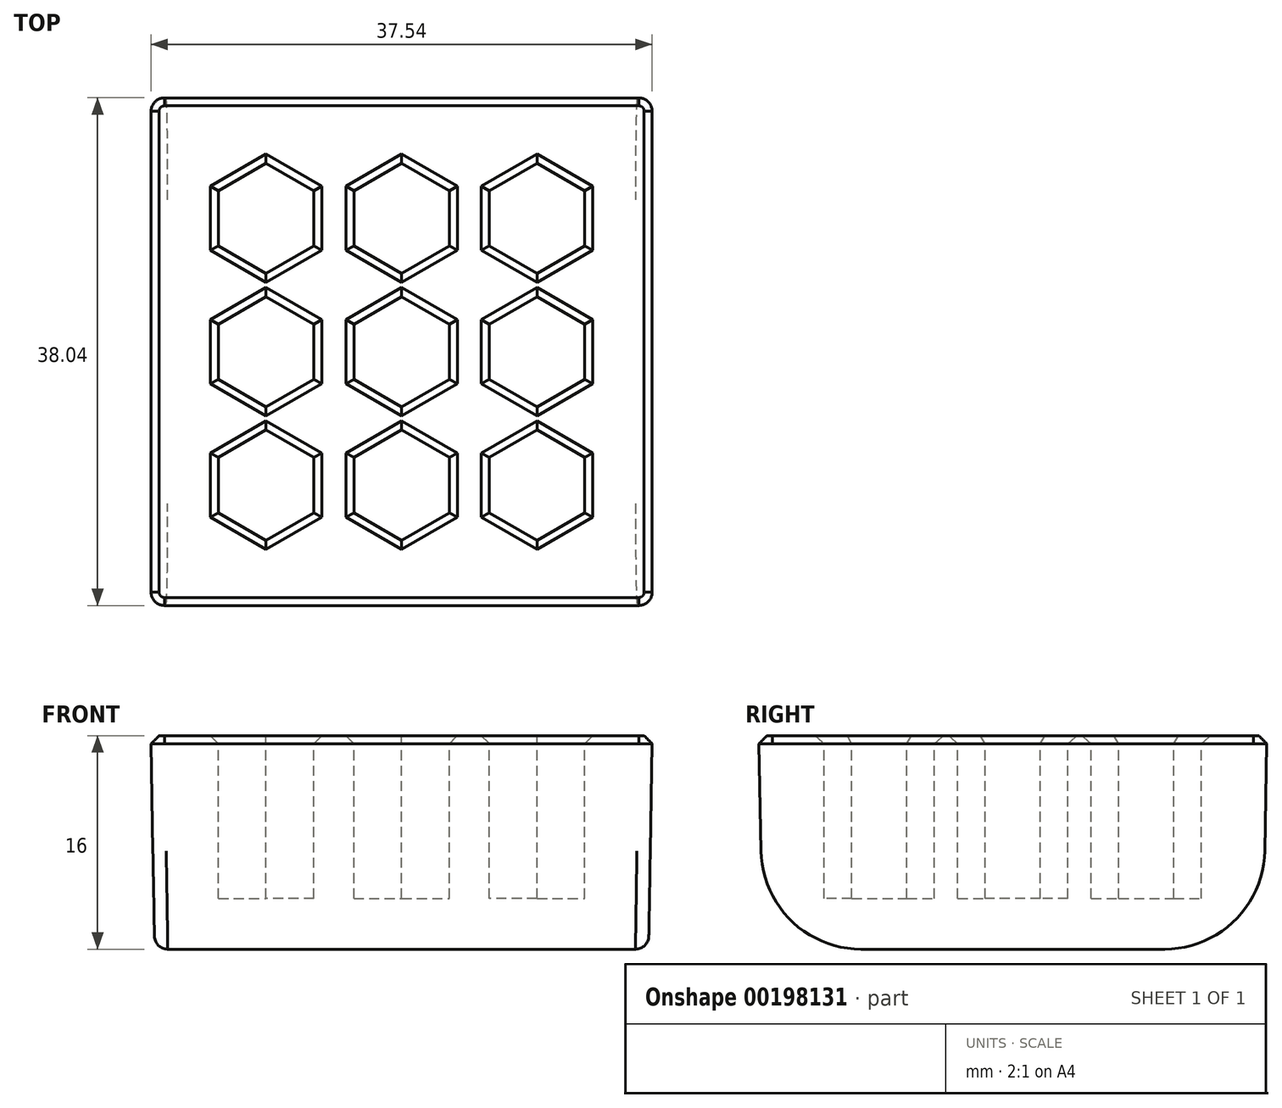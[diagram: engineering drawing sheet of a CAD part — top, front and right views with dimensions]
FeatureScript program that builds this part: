
annotation { "Feature Type Name" : "Feature", "Feature Type Description" : "" }
export const myFeature = defineFeature(function(context is Context, id is Id, definition is map)
    precondition{}
    {
        {
            var Q0;
            Q0=qCreatedBy(makeId("Top.planeOp"),FACE);
            var sketch = newSketch(context, id + "F0", { "sketchPlane" : qUnion([Q0])});
            skLineSegment(sketch, "E0.bottom", {"start": v(18.5, 18.75) * mm, "end": v(-18.5, 18.75) * mm});
            skLineSegment(sketch, "E0.top", {"start": v(18.5, -18.75) * mm, "end": v(-18.5, -18.75) * mm});
            skLineSegment(sketch, "E0.left", {"start": v(18.5, 18.75) * mm, "end": v(18.5, -18.75) * mm});
            skLineSegment(sketch, "E0.right", {"start": v(-18.5, 18.75) * mm, "end": v(-18.5, -18.75) * mm});
            skPoint(sketch, "E0.middle", {"position": v(0, 0) * mm});
            skSolve(sketch);
        }
        {
            var Q0;
            Q0=makeQuery(id+"F0.imprint","IMPRINT",FACE,{"disambiguationData":[TD([[makeQuery(id+"F0.imprint","IMPRINT",EDGE,{"derivedFrom":sQuery(id+"F0.wireOp",EDGE,"E0.bottom")}),1.0]])]});
            extrude(context, id + "F1", {"entities" : qUnion([Q0]), "depth" : (25 - 13 + 4) * mm, "hasDraft" : true, "draftAngle" : 1 * degree});
        }
        {
            var Q0;
            Q0=makeQuery(id+"F1.opExtrude","CAP_EDGE",EDGE,{"disambiguationData":[OSD([sQuery(id+"F0.wireOp",EDGE,"E0.top")])],"isStart":true});
            var Q1;
            Q1=makeQuery(id+"F1.opExtrude","CAP_EDGE",EDGE,{"disambiguationData":[OSD([sQuery(id+"F0.wireOp",EDGE,"E0.bottom")])],"isStart":true});
            fillet(context, id + "F2", {"entities" : qUnion([Q0, Q1]), "radius" : 7.5 * mm, "tangentPropagation" : true, "allowEdgeOverflow" : false});
        }
        {
            var Q0;
            Q0=makeQuery(id+"F1.opExtrude","SWEPT_EDGE",EDGE,{"disambiguationData":[OSD([sQuery(id+"F0.wireOp",EDGE,"E0.top"),sQuery(id+"F0.wireOp",EDGE,"E0.left")])]});
            var Q1;
            Q1=makeQuery(id+"F1.opExtrude","SWEPT_EDGE",EDGE,{"disambiguationData":[OSD([sQuery(id+"F0.wireOp",EDGE,"E0.top"),sQuery(id+"F0.wireOp",EDGE,"E0.right")])]});
            fillet(context, id + "F3", {"entities" : qUnion([Q0, Q1]), "radius" : 1 * mm, "tangentPropagation" : true, "allowEdgeOverflow" : false});
        }
        {
            var Q0;
            Q0=makeQuery(id+"F1.opExtrude","CAP_FACE",FACE,{"disambiguationData":[OSD([sQuery(id+"F0.wireOp",EDGE,"E0.bottom"),sQuery(id+"F0.wireOp",EDGE,"E0.top"),sQuery(id+"F0.wireOp",EDGE,"E0.left"),sQuery(id+"F0.wireOp",EDGE,"E0.right")])],"isStart":false});
            var sketch = newSketch(context, id + "F4", { "sketchPlane" : qUnion([Q0])});
            skLineSegment(sketch, "E1", {"start": v(0, 19.03) * mm, "end": v(0, -19.03) * mm, "construction": true});
            skLineSegment(sketch, "E2", {"start": v(-18.78, 0) * mm, "end": v(18.78, 0) * mm, "construction": true});
            skCircle(sketch, "E3.cCircle", {"center": v(0, 0) * mm, "radius": 3.57 * mm, "construction": true});
            skLineSegment(sketch, "E3.0", {"start": v(3.58, 2.06) * mm, "end": v(3.58, -2.06) * mm});
            skLineSegment(sketch, "E3.1", {"start": v(3.58, -2.06) * mm, "end": v(0, -4.13) * mm});
            skLineSegment(sketch, "E3.2", {"start": v(0, -4.13) * mm, "end": v(-3.57, -2.06) * mm});
            skLineSegment(sketch, "E3.3", {"start": v(-3.57, -2.06) * mm, "end": v(-3.57, 2.06) * mm});
            skLineSegment(sketch, "E3.4", {"start": v(-3.57, 2.06) * mm, "end": v(0, 4.13) * mm});
            skLineSegment(sketch, "E3.5", {"start": v(0, 4.13) * mm, "end": v(3.58, 2.06) * mm});
            skPoint(sketch, "E3.0.midPoint", {"position": v(3.58, 0) * mm});
            skLineSegment(sketch, "E4.0.1.0", {"start": v(-3.57, 12.06) * mm, "end": v(0, 14.13) * mm});
            skLineSegment(sketch, "E4.0.1.1", {"start": v(-3.57, 7.94) * mm, "end": v(-3.57, 12.06) * mm});
            skLineSegment(sketch, "E4.0.1.2", {"start": v(0, 5.87) * mm, "end": v(-3.57, 7.94) * mm});
            skCircle(sketch, "E4.0.1.3", {"center": v(0, 10) * mm, "radius": 3.57 * mm, "construction": true});
            skLineSegment(sketch, "E4.0.1.4", {"start": v(3.58, 7.94) * mm, "end": v(0, 5.87) * mm});
            skLineSegment(sketch, "E4.0.1.5", {"start": v(3.58, 12.06) * mm, "end": v(3.58, 7.94) * mm});
            skLineSegment(sketch, "E4.0.1.6", {"start": v(0, 14.13) * mm, "end": v(3.58, 12.06) * mm});
            skLineSegment(sketch, "E4.1.0.0", {"start": v(6.57, 2.06) * mm, "end": v(10.15, 4.13) * mm});
            skLineSegment(sketch, "E4.1.0.1", {"start": v(6.58, -2.06) * mm, "end": v(6.58, 2.06) * mm});
            skLineSegment(sketch, "E4.1.0.2", {"start": v(10.15, -4.13) * mm, "end": v(6.58, -2.06) * mm});
            skCircle(sketch, "E4.1.0.3", {"center": v(10.15, 0) * mm, "radius": 3.57 * mm, "construction": true});
            skLineSegment(sketch, "E4.1.0.4", {"start": v(13.73, -2.06) * mm, "end": v(10.15, -4.13) * mm});
            skLineSegment(sketch, "E4.1.0.5", {"start": v(13.73, 2.06) * mm, "end": v(13.73, -2.06) * mm});
            skLineSegment(sketch, "E4.1.0.6", {"start": v(10.15, 4.13) * mm, "end": v(13.73, 2.06) * mm});
            skLineSegment(sketch, "E4.1.1.0", {"start": v(6.57, 12.06) * mm, "end": v(10.15, 14.13) * mm});
            skLineSegment(sketch, "E4.1.1.1", {"start": v(6.58, 7.94) * mm, "end": v(6.58, 12.06) * mm});
            skLineSegment(sketch, "E4.1.1.2", {"start": v(10.15, 5.87) * mm, "end": v(6.58, 7.94) * mm});
            skCircle(sketch, "E4.1.1.3", {"center": v(10.15, 10) * mm, "radius": 3.57 * mm, "construction": true});
            skLineSegment(sketch, "E4.1.1.4", {"start": v(13.73, 7.94) * mm, "end": v(10.15, 5.87) * mm});
            skLineSegment(sketch, "E4.1.1.5", {"start": v(13.73, 12.06) * mm, "end": v(13.73, 7.94) * mm});
            skLineSegment(sketch, "E4.1.1.6", {"start": v(10.15, 14.13) * mm, "end": v(13.73, 12.06) * mm});
            skLineSegment(sketch, "E4.direction1", {"start": v(-3.57, 2.06) * mm, "end": v(6.58, 2.06) * mm, "construction": true});
            skLineSegment(sketch, "E4.direction2", {"start": v(-3.57, 2.06) * mm, "end": v(-3.57, 12.06) * mm, "construction": true});
            skLineSegment(sketch, "E5.MirrorCS", {"start": v(-6.57, 7.94) * mm, "end": v(-6.57, 12.06) * mm});
            skLineSegment(sketch, "E6.MirrorCS", {"start": v(-6.57, 12.06) * mm, "end": v(-10.15, 14.13) * mm});
            skCircle(sketch, "E7.MirrorC", {"center": v(-10.15, 10) * mm, "radius": 3.57 * mm, "construction": true});
            skLineSegment(sketch, "E8.MirrorCS", {"start": v(-10.15, 14.13) * mm, "end": v(-13.72, 12.06) * mm});
            skLineSegment(sketch, "E9.MirrorCS", {"start": v(-13.72, 12.06) * mm, "end": v(-13.72, 7.94) * mm});
            skLineSegment(sketch, "E10.MirrorCS", {"start": v(-13.72, 7.94) * mm, "end": v(-10.15, 5.87) * mm});
            skLineSegment(sketch, "E11.MirrorCS", {"start": v(-10.15, 5.87) * mm, "end": v(-6.58, 7.94) * mm});
            skLineSegment(sketch, "E12.MirrorCS", {"start": v(-6.57, 2.06) * mm, "end": v(-10.15, 4.13) * mm});
            skLineSegment(sketch, "E13.MirrorCS", {"start": v(-10.15, 4.13) * mm, "end": v(-13.72, 2.06) * mm});
            skCircle(sketch, "E14.MirrorC", {"center": v(-10.15, 0) * mm, "radius": 3.57 * mm, "construction": true});
            skLineSegment(sketch, "E15.MirrorCS", {"start": v(-13.72, 2.06) * mm, "end": v(-13.72, -2.06) * mm});
            skLineSegment(sketch, "E16.MirrorCS", {"start": v(-13.72, -2.06) * mm, "end": v(-10.15, -4.13) * mm});
            skLineSegment(sketch, "E17.MirrorCS", {"start": v(-10.15, -4.13) * mm, "end": v(-6.58, -2.06) * mm});
            skLineSegment(sketch, "E18.MirrorCS", {"start": v(-6.57, -2.06) * mm, "end": v(-6.57, 2.06) * mm});
            skCircle(sketch, "E19.MirrorC", {"center": v(-10.15, -10) * mm, "radius": 3.57 * mm, "construction": true});
            skLineSegment(sketch, "E20.MirrorCS", {"start": v(-13.72, -7.94) * mm, "end": v(-10.15, -5.87) * mm});
            skLineSegment(sketch, "E21.MirrorCS", {"start": v(-10.15, -5.87) * mm, "end": v(-6.57, -7.94) * mm});
            skLineSegment(sketch, "E22.MirrorCS", {"start": v(-6.57, -7.94) * mm, "end": v(-6.57, -12.06) * mm});
            skLineSegment(sketch, "E23.MirrorCS", {"start": v(-6.58, -12.06) * mm, "end": v(-10.15, -14.13) * mm});
            skLineSegment(sketch, "E24.MirrorCS", {"start": v(-10.15, -14.13) * mm, "end": v(-13.72, -12.06) * mm});
            skLineSegment(sketch, "E25.MirrorCS", {"start": v(-13.72, -12.06) * mm, "end": v(-13.72, -7.94) * mm});
            skLineSegment(sketch, "E26.MirrorCS", {"start": v(6.58, -7.94) * mm, "end": v(6.58, -12.06) * mm});
            skLineSegment(sketch, "E27.MirrorCS", {"start": v(6.58, -12.06) * mm, "end": v(10.15, -14.13) * mm});
            skLineSegment(sketch, "E28.MirrorCS", {"start": v(10.15, -14.13) * mm, "end": v(13.73, -12.06) * mm});
            skCircle(sketch, "E29.MirrorC", {"center": v(10.15, -10) * mm, "radius": 3.57 * mm, "construction": true});
            skLineSegment(sketch, "E30.MirrorCS", {"start": v(13.73, -12.06) * mm, "end": v(13.73, -7.94) * mm});
            skLineSegment(sketch, "E31.MirrorCS", {"start": v(13.73, -7.94) * mm, "end": v(10.15, -5.87) * mm});
            skLineSegment(sketch, "E32.MirrorCS", {"start": v(10.15, -5.87) * mm, "end": v(6.57, -7.94) * mm});
            skCircle(sketch, "E33.MirrorC", {"center": v(0, -10) * mm, "radius": 3.57 * mm, "construction": true});
            skLineSegment(sketch, "E34.MirrorCS", {"start": v(3.58, -7.94) * mm, "end": v(0, -5.87) * mm});
            skLineSegment(sketch, "E35.MirrorCS", {"start": v(0, -5.87) * mm, "end": v(-3.57, -7.94) * mm});
            skLineSegment(sketch, "E36.MirrorCS", {"start": v(-3.57, -2.06) * mm, "end": v(-3.57, -12.06) * mm, "construction": true});
            skLineSegment(sketch, "E37.MirrorCS", {"start": v(-3.57, -12.06) * mm, "end": v(0, -14.13) * mm});
            skLineSegment(sketch, "E38.MirrorCS", {"start": v(0, -14.13) * mm, "end": v(3.58, -12.06) * mm});
            skLineSegment(sketch, "E39.MirrorCS", {"start": v(3.58, -12.06) * mm, "end": v(3.58, -7.94) * mm});
            skLineSegment(sketch, "E40", {"start": v(-3.57, -7.94) * mm, "end": v(-3.57, -12.06) * mm});
            skSolve(sketch);
        }
        {
            var Q0;
            Q0 = qSketchRegion(id + "F4", true);
            extrude(context, id + "F5", {"entities" : qUnion([Q0]), "operationType" : NewBodyOperationType.REMOVE, "oppositeDirection" : true, "depth" : 12.2 * mm});
        }
        {
            var Q0;
            Q0=makeQuery(id+"F1.opExtrude","CAP_FACE",FACE,{"disambiguationData":[OSD([sQuery(id+"F0.wireOp",EDGE,"E0.bottom"),sQuery(id+"F0.wireOp",EDGE,"E0.top"),sQuery(id+"F0.wireOp",EDGE,"E0.left"),sQuery(id+"F0.wireOp",EDGE,"E0.right")])],"isStart":false});
            chamfer(context, id + "F6", {"entities" : qUnion([Q0]), "width" : .6 * mm, "tangentPropagation" : true});
        }
    });
